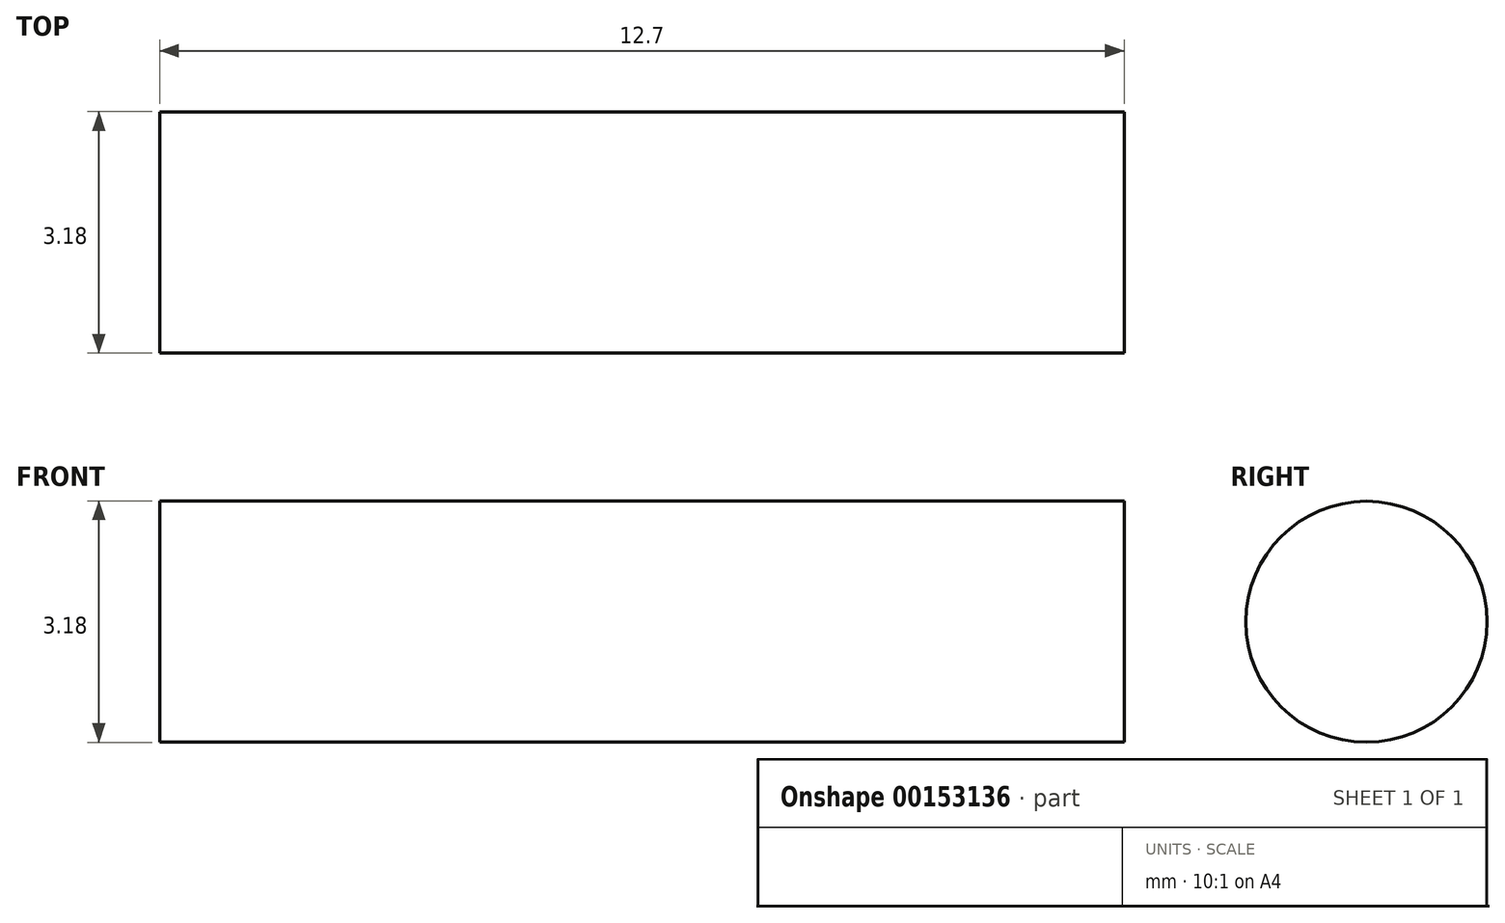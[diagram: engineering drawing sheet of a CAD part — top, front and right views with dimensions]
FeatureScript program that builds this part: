
annotation { "Feature Type Name" : "Feature", "Feature Type Description" : "" }
export const myFeature = defineFeature(function(context is Context, id is Id, definition is map)
    precondition{}
    {
        {
            var Q0;
            Q0=qCreatedBy(makeId("Right.planeOp"),FACE);
            var sketch = newSketch(context, id + "F1", { "sketchPlane" : qUnion([Q0])});
            skCircle(sketch, "E0", {"center": v(0, 0) * mm, "radius": 1.59 * mm});
            skSolve(sketch);
        }
        {
            var Q0;
            Q0=makeQuery(id+"F1.imprint","IMPRINT",FACE,{"disambiguationData":[TD([[makeQuery(id+"F1.imprint","IMPRINT",EDGE,{"derivedFrom":sQuery(id+"F1.wireOp",EDGE,"E0")}),1.0]])]});
            extrude(context, id + "F0", {"entities" : qUnion([Q0]), "depth" : 12.7 * mm});
        }
    });
